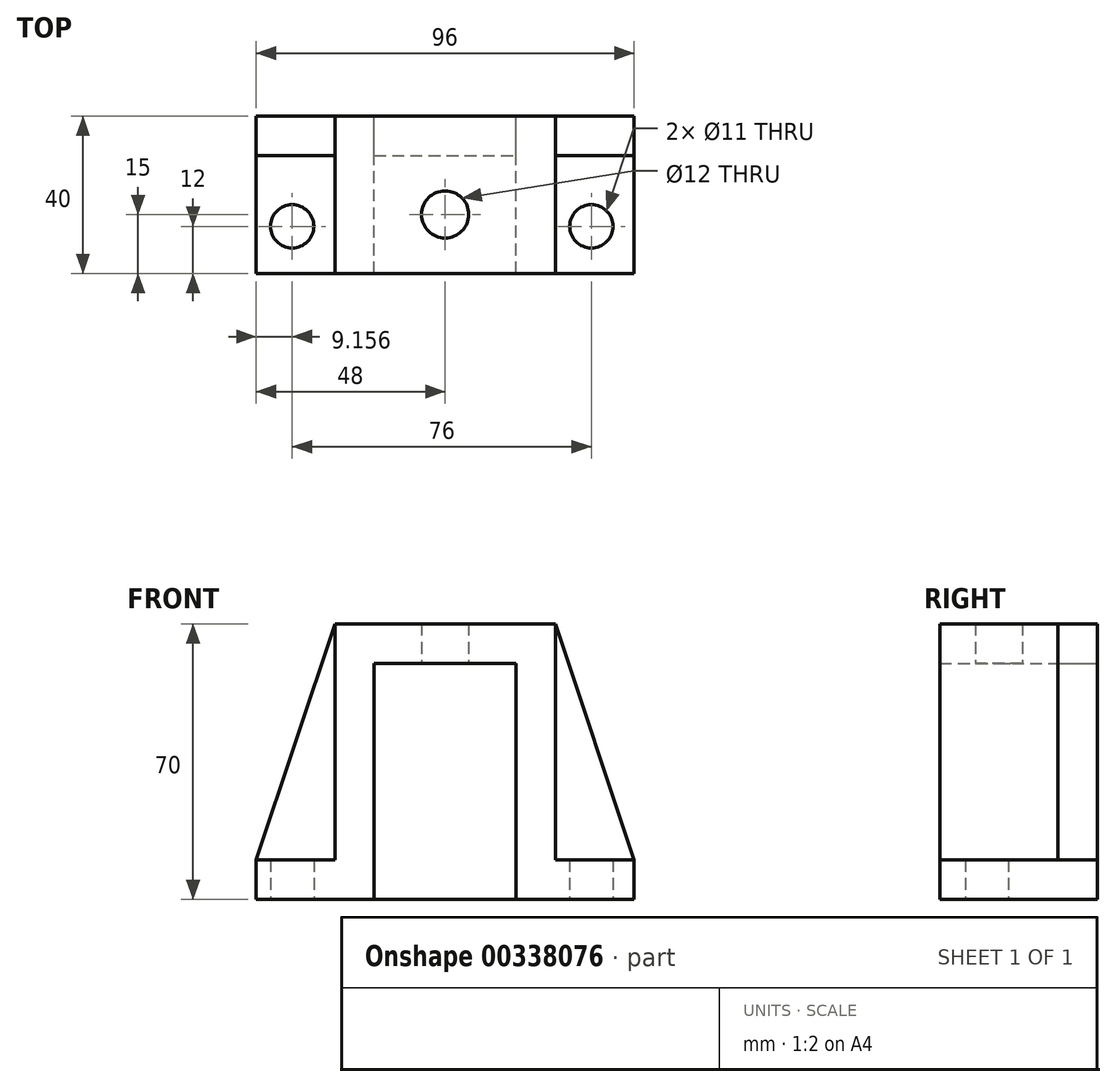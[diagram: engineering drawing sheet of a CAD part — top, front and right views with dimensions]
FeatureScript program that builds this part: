
annotation { "Feature Type Name" : "Feature", "Feature Type Description" : "" }
export const myFeature = defineFeature(function(context is Context, id is Id, definition is map)
    precondition{}
    {
        {
            var Q0;
            Q0=qCreatedBy(makeId("Front.planeOp"),FACE);
            var sketch = newSketch(context, id + "F0", { "sketchPlane" : qUnion([Q0])});
            skLineSegment(sketch, "E0", {"start": v(30, 0) * mm, "end": v(0, 0) * mm});
            skLineSegment(sketch, "E1", {"start": v(0, 0) * mm, "end": v(0, 10) * mm});
            skLineSegment(sketch, "E2", {"start": v(0, 10) * mm, "end": v(20, 70) * mm});
            skLineSegment(sketch, "E3", {"start": v(20, 70) * mm, "end": v(20, 10) * mm});
            skLineSegment(sketch, "E4", {"start": v(20, 10) * mm, "end": v(0, 10) * mm});
            skLineSegment(sketch, "E5", {"start": v(30, 0) * mm, "end": v(30, 60) * mm});
            skLineSegment(sketch, "E6", {"start": v(30, 60) * mm, "end": v(66, 60) * mm});
            skLineSegment(sketch, "E7", {"start": v(66, 60) * mm, "end": v(66, 0) * mm});
            skLineSegment(sketch, "E8", {"start": v(66, 0) * mm, "end": v(96, 0) * mm});
            skLineSegment(sketch, "E9", {"start": v(96, 0) * mm, "end": v(96, 10) * mm});
            skLineSegment(sketch, "E10", {"start": v(96, 10) * mm, "end": v(76, 70) * mm});
            skLineSegment(sketch, "E11", {"start": v(76, 70) * mm, "end": v(76, 10) * mm});
            skLineSegment(sketch, "E12", {"start": v(20, 70) * mm, "end": v(76, 70) * mm});
            skLineSegment(sketch, "E13", {"start": v(76, 10) * mm, "end": v(96, 10) * mm});
            skLineSegment(sketch, "E14", {"start": v(30, 0) * mm, "end": v(66, 0) * mm});
            skSolve(sketch);
        }
        {
            var Q0;
            Q0=makeQuery(id+"F0.imprint","IMPRINT",FACE,{"disambiguationData":[TD([[makeQuery(id+"F0.imprint","IMPRINT",EDGE,{"derivedFrom":sQuery(id+"F0.wireOp",EDGE,"E5")}),-1.0]])]});
            var Q1;
            Q1=makeQuery(id+"F0.imprint","IMPRINT",FACE,{"disambiguationData":[TD([[makeQuery(id+"F0.imprint","IMPRINT",EDGE,{"derivedFrom":sQuery(id+"F0.wireOp",EDGE,"E10")}),1.0]])]});
            var Q2;
            Q2=makeQuery(id+"F0.imprint","IMPRINT",FACE,{"disambiguationData":[TD([[makeQuery(id+"F0.imprint","IMPRINT",EDGE,{"derivedFrom":sQuery(id+"F0.wireOp",EDGE,"E2")}),-1.0]])]});
            extrude(context, id + "F1", {"entities" : qUnion([Q0, Q1, Q2]), "depth" : 10 * mm});
        }
        {
            var Q0;
            Q0=qCreatedBy(makeId("Top.planeOp"),FACE);
            var sketch = newSketch(context, id + "F2", { "sketchPlane" : qUnion([Q0])});
            skLineSegment(sketch, "E15", {"start": v(20, 0) * mm, "end": v(20, -40) * mm});
            skLineSegment(sketch, "E16", {"start": v(76, 0) * mm, "end": v(76, -40) * mm});
            skLineSegment(sketch, "E17", {"start": v(76, -40) * mm, "end": v(20, -40) * mm});
            skCircle(sketch, "E18", {"center": v(48, -25) * mm, "radius": 5 * mm});
            skLineSegment(sketch, "E19", {"start": v(20, 0) * mm, "end": v(76, 0) * mm});
            skLineSegment(sketch, "E20", {"start": v(-0.84, 0) * mm, "end": v(-0.84, -40) * mm});
            skLineSegment(sketch, "E21", {"start": v(95.16, 0) * mm, "end": v(95.16, -40) * mm});
            skLineSegment(sketch, "E22", {"start": v(0, -40) * mm, "end": v(95.16, -40) * mm});
            skCircle(sketch, "E23", {"center": v(9.16, -28) * mm, "radius": 5.5 * mm});
            skCircle(sketch, "E24", {"center": v(85.16, -28) * mm, "radius": 5.5 * mm});
            skSolve(sketch);
        }
        {
            var Q0;
            Q0=makeQuery(id+"F0.imprint","IMPRINT",FACE,{"disambiguationData":[TD([[makeQuery(id+"F0.imprint","IMPRINT",EDGE,{"derivedFrom":sQuery(id+"F0.wireOp",EDGE,"E0")}),-1.0]])]});
            extrude(context, id + "F3", {"entities" : qUnion([Q0]), "depth" : 40 * mm});
        }
        {
            var Q0;
            Q0=sQuery(id+"F2.wireOp",VERTEX,"E23.center");
            var Q1;
            Q1=sQuery(id+"F2.wireOp",VERTEX,"E24.center");
            var Q2;
            Q2=makeQuery(id+"F3.opExtrude","SWEPT_BODY",BODY,{"disambiguationData":[OSD([sQuery(id+"F0.wireOp",EDGE,"E0"),sQuery(id+"F0.wireOp",EDGE,"E1"),sQuery(id+"F0.wireOp",EDGE,"E3"),sQuery(id+"F0.wireOp",EDGE,"E4"),sQuery(id+"F0.wireOp",EDGE,"E5"),sQuery(id+"F0.wireOp",EDGE,"E6"),sQuery(id+"F0.wireOp",EDGE,"E7"),sQuery(id+"F0.wireOp",EDGE,"E8"),sQuery(id+"F0.wireOp",EDGE,"E9"),sQuery(id+"F0.wireOp",EDGE,"E11"),sQuery(id+"F0.wireOp",EDGE,"E12"),sQuery(id+"F0.wireOp",EDGE,"E13")])]});
            hole(context, id + "F4", {"style" : HoleStyle.SIMPLE, "endStyle" : HoleEndStyle.THROUGH, "oppositeDirection" : true, "holeDiameter" : 11 * mm, "tappedDepth" : 12 * mm, "tapClearance" : 3, "locations" : qUnion([Q0, Q1]), "scope" : qUnion([Q2])});
        }
        {
            var Q0;
            Q0=sQuery(id+"F2.wireOp",VERTEX,"E18.center");
            var Q1;
            Q1=makeQuery(id+"F3.opExtrude","SWEPT_BODY",BODY,{"disambiguationData":[OSD([sQuery(id+"F0.wireOp",EDGE,"E0"),sQuery(id+"F0.wireOp",EDGE,"E1"),sQuery(id+"F0.wireOp",EDGE,"E3"),sQuery(id+"F0.wireOp",EDGE,"E4"),sQuery(id+"F0.wireOp",EDGE,"E5"),sQuery(id+"F0.wireOp",EDGE,"E6"),sQuery(id+"F0.wireOp",EDGE,"E7"),sQuery(id+"F0.wireOp",EDGE,"E8"),sQuery(id+"F0.wireOp",EDGE,"E9"),sQuery(id+"F0.wireOp",EDGE,"E11"),sQuery(id+"F0.wireOp",EDGE,"E12"),sQuery(id+"F0.wireOp",EDGE,"E13")])]});
            hole(context, id + "F5", {"style" : HoleStyle.SIMPLE, "endStyle" : HoleEndStyle.THROUGH, "oppositeDirection" : true, "holeDiameter" : 12 * mm, "tappedDepth" : 12 * mm, "tapClearance" : 3, "locations" : qUnion([Q0]), "scope" : qUnion([Q1])});
        }
    });
